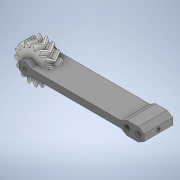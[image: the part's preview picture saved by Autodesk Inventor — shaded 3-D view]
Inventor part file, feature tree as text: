
AUTODESK INVENTOR PART (.ipt)
format: ipt  version: 2020 (Build 240168000, 168)  size: 964,608 bytes
history: native  units: in
note: dims shown in document units (in); Inventor stores cm internally (conversion verified against a paired STEP export)
features: sketch x4, other x3, extrude x3, plane x2, mirror x1, projected_geometry x1
ambient origin geometry x8: Origin, YZ Plane, XZ Plane, XY Plane, X Axis, Y Axis, Z Axis, Center Point
bodies: Solid1 (feature_tree), Solid2 (feature_tree)
feature tree (14):
  other  "Spur Gear1"
  plane  "Work Plane3"
  extrude  "Extrusion1"  Depth=3.4256in
  plane  "Work Plane1"
  extrude  "Extrusion2"  Depth=0.7874in
  sketch  "Sketch4"  dims[d4=0.0in d5=0.0906in]
  extrude  "Extrusion4"  Depth=0.0906in
  mirror  "Mirror3"
  sketch  "Sketch1"  dims[d0=0.1818in d1=3.4256in]
  sketch  "Sketch2"  dims[d2=0.0945in d3=0.7874in]
  sketch  "Sketch5"  dims[d6=0.7874in d7=0.0in d29=0.315in d31=0.315in d33=0.1476in d34=0.2362in d35=0.0in d38=0.315in d69=2.4807in d70=0.3937in d71=0.1969in]
  other  "Solid1::Spur Gear1"
  other  "TaggingFeature1"
  projected_geometry  "Projected Loop11"
